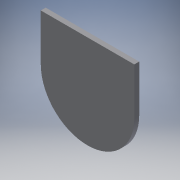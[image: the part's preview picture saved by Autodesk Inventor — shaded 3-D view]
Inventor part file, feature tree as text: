
AUTODESK INVENTOR PART (.ipt)
format: ipt  version: 2016 (Build 200138000, 138)  size: 100,352 bytes
history: native  units: in
note: dims shown in document units (in); Inventor stores cm internally (conversion verified against a paired STEP export)
features: reference x2, extrude x1, sketch x1
ambient origin geometry x8: Origin, YZ Plane, XZ Plane, XY Plane, X Axis, Y Axis, Z Axis, Center Point
bodies: Solid1 (feature_tree)
feature tree (4):
  extrude  "Extrusion1"  Depth=3.0in
  sketch  "Sketch1"  dims[d0=1.0in d1=3.0in d2=0.1575in d3=0.0in]
  reference  "Reference1"
  reference  "Reference2"
